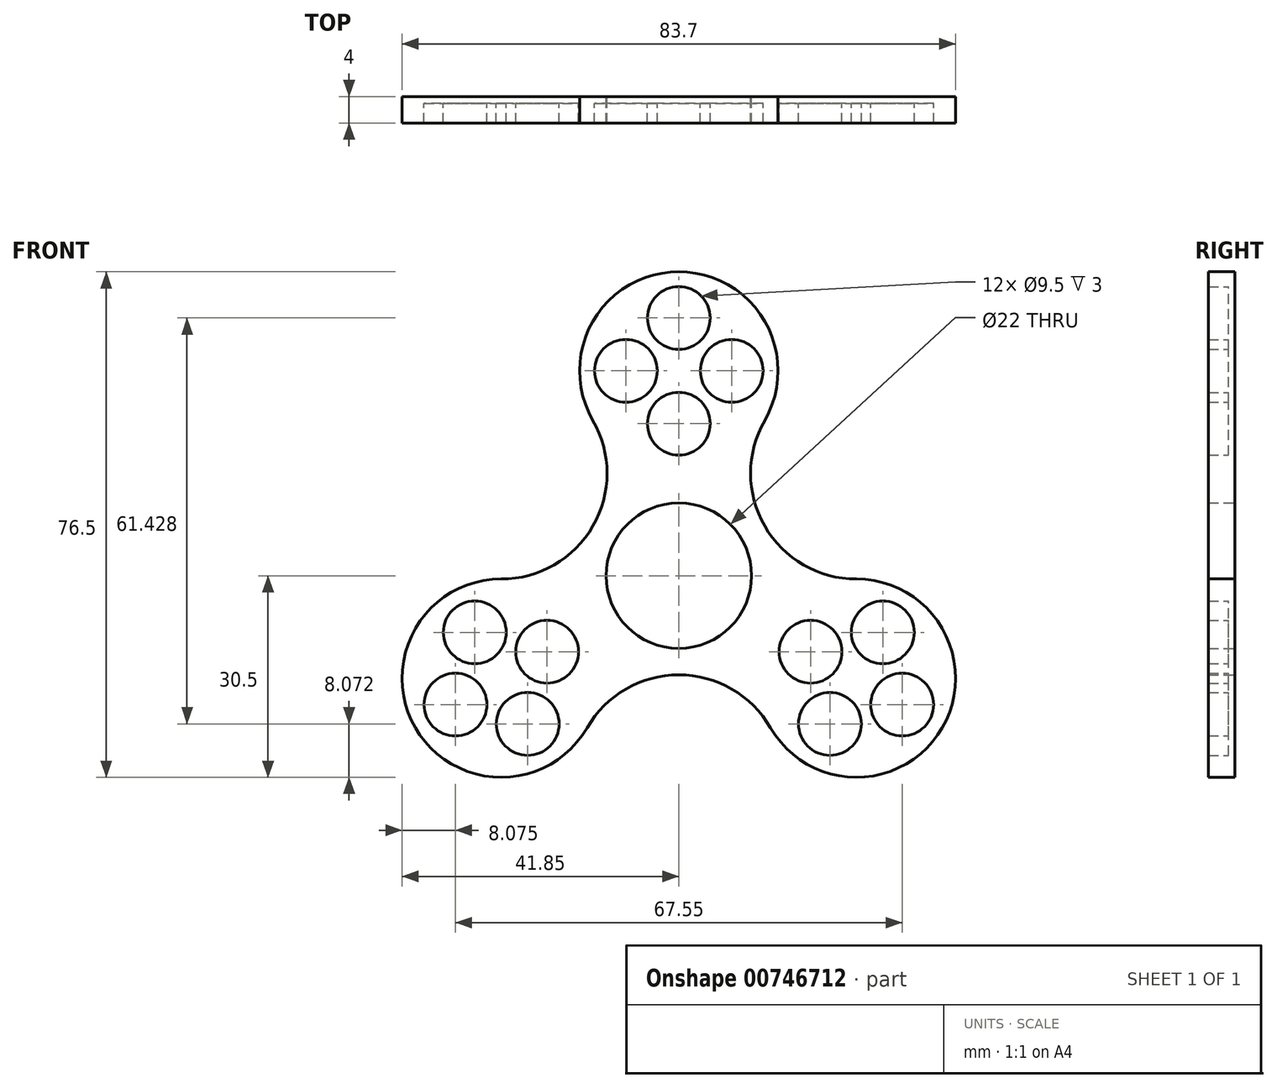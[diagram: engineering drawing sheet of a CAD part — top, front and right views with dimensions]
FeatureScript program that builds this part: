
annotation { "Feature Type Name" : "Feature", "Feature Type Description" : "" }
export const myFeature = defineFeature(function(context is Context, id is Id, definition is map)
    precondition{}
    {
        {
            var Q0;
            Q0=qCreatedBy(makeId("Front.planeOp"),FACE);
            var sketch = newSketch(context, id + "F0", { "sketchPlane" : qUnion([Q0])});
            skCircle(sketch, "E0", {"center": v(0, 0) * mm, "radius": 11 * mm});
            skArc(sketch, "E1.1.0", {"start": v(-26.85, -0.5) * mm, "mid": v(-39.84, -23) * mm, "end": v(-13.86, -23) * mm});
            skArc(sketch, "E1.2.0", {"start": v(13.86, -23) * mm, "mid": v(39.84, -23) * mm, "end": v(26.85, -0.5) * mm});
            skArc(sketch, "E2", {"start": v(-26.85, -0.5) * mm, "mid": v(-13, 7.5) * mm, "end": v(-13, 23.5) * mm});
            skArc(sketch, "E3.1.0", {"start": v(13.86, -23) * mm, "mid": v(0, -15) * mm, "end": v(-13.86, -23) * mm});
            skArc(sketch, "E3.2.0", {"start": v(13, 23.5) * mm, "mid": v(13, 7.5) * mm, "end": v(26.85, -0.5) * mm});
            skCircle(sketch, "E4", {"center": v(0, 23) * mm, "radius": 4.75 * mm});
            skCircle(sketch, "E5.1.0", {"center": v(8, 31) * mm, "radius": 4.75 * mm});
            skCircle(sketch, "E5.2.0", {"center": v(0, 39) * mm, "radius": 4.75 * mm});
            skCircle(sketch, "E5.3.0", {"center": v(-8, 31) * mm, "radius": 4.75 * mm});
            skPoint(sketch, "E5.center", {"position": v(0, 31) * mm});
            skCircle(sketch, "E6.1.0", {"center": v(-22.85, -22.43) * mm, "radius": 4.75 * mm});
            skCircle(sketch, "E6.1.1", {"center": v(-33.77, -19.5) * mm, "radius": 4.75 * mm});
            skCircle(sketch, "E6.1.2", {"center": v(-19.92, -11.5) * mm, "radius": 4.75 * mm});
            skCircle(sketch, "E6.1.3", {"center": v(-30.85, -8.57) * mm, "radius": 4.75 * mm});
            skCircle(sketch, "E6.2.0", {"center": v(30.85, -8.57) * mm, "radius": 4.75 * mm});
            skCircle(sketch, "E6.2.1", {"center": v(33.77, -19.5) * mm, "radius": 4.75 * mm});
            skCircle(sketch, "E6.2.2", {"center": v(19.92, -11.5) * mm, "radius": 4.75 * mm});
            skCircle(sketch, "E6.2.3", {"center": v(22.85, -22.43) * mm, "radius": 4.75 * mm});
            skArc(sketch, "E7", {"start": v(13, 23.5) * mm, "mid": v(0, 46) * mm, "end": v(-13, 23.5) * mm});
            skSolve(sketch);
        }
        {
            var Q0;
            Q0 = qSketchRegion(id + "F0", true);
            extrude(context, id + "F1", {"entities" : qUnion([Q0]), "depth" : 4 * mm, "offsetDistance" : 25 * mm});
        }
        {
            var Q0;
            Q0=makeQuery(id+"F0.imprint","IMPRINT",FACE,{"disambiguationData":[TD([[makeQuery(id+"F0.imprint","IMPRINT",EDGE,{"derivedFrom":sQuery(id+"F0.wireOp",EDGE,"E5.3.0")}),1.0]])]});
            var Q1;
            Q1=makeQuery(id+"F0.imprint","IMPRINT",FACE,{"disambiguationData":[TD([[makeQuery(id+"F0.imprint","IMPRINT",EDGE,{"derivedFrom":sQuery(id+"F0.wireOp",EDGE,"E5.2.0")}),1.0]])]});
            var Q2;
            Q2=makeQuery(id+"F0.imprint","IMPRINT",FACE,{"disambiguationData":[TD([[makeQuery(id+"F0.imprint","IMPRINT",EDGE,{"derivedFrom":sQuery(id+"F0.wireOp",EDGE,"E5.1.0")}),1.0]])]});
            var Q3;
            Q3=makeQuery(id+"F0.imprint","IMPRINT",FACE,{"disambiguationData":[TD([[makeQuery(id+"F0.imprint","IMPRINT",EDGE,{"derivedFrom":sQuery(id+"F0.wireOp",EDGE,"E4")}),1.0]])]});
            var Q4;
            Q4=makeQuery(id+"F0.imprint","IMPRINT",FACE,{"disambiguationData":[TD([[makeQuery(id+"F0.imprint","IMPRINT",EDGE,{"derivedFrom":sQuery(id+"F0.wireOp",EDGE,"E6.1.3")}),1.0]])]});
            var Q5;
            Q5=makeQuery(id+"F0.imprint","IMPRINT",FACE,{"disambiguationData":[TD([[makeQuery(id+"F0.imprint","IMPRINT",EDGE,{"derivedFrom":sQuery(id+"F0.wireOp",EDGE,"E6.1.1")}),1.0]])]});
            var Q6;
            Q6=makeQuery(id+"F0.imprint","IMPRINT",FACE,{"disambiguationData":[TD([[makeQuery(id+"F0.imprint","IMPRINT",EDGE,{"derivedFrom":sQuery(id+"F0.wireOp",EDGE,"E6.1.0")}),1.0]])]});
            var Q7;
            Q7=makeQuery(id+"F0.imprint","IMPRINT",FACE,{"disambiguationData":[TD([[makeQuery(id+"F0.imprint","IMPRINT",EDGE,{"derivedFrom":sQuery(id+"F0.wireOp",EDGE,"E6.1.2")}),1.0]])]});
            var Q8;
            Q8=makeQuery(id+"F0.imprint","IMPRINT",FACE,{"disambiguationData":[TD([[makeQuery(id+"F0.imprint","IMPRINT",EDGE,{"derivedFrom":sQuery(id+"F0.wireOp",EDGE,"E6.2.3")}),1.0]])]});
            var Q9;
            Q9=makeQuery(id+"F0.imprint","IMPRINT",FACE,{"disambiguationData":[TD([[makeQuery(id+"F0.imprint","IMPRINT",EDGE,{"derivedFrom":sQuery(id+"F0.wireOp",EDGE,"E6.2.2")}),1.0]])]});
            var Q10;
            Q10=makeQuery(id+"F0.imprint","IMPRINT",FACE,{"disambiguationData":[TD([[makeQuery(id+"F0.imprint","IMPRINT",EDGE,{"derivedFrom":sQuery(id+"F0.wireOp",EDGE,"E6.2.0")}),1.0]])]});
            var Q11;
            Q11=makeQuery(id+"F0.imprint","IMPRINT",FACE,{"disambiguationData":[TD([[makeQuery(id+"F0.imprint","IMPRINT",EDGE,{"derivedFrom":sQuery(id+"F0.wireOp",EDGE,"E6.2.1")}),1.0]])]});
            extrude(context, id + "F2", {"entities" : qUnion([Q0, Q1, Q2, Q3, Q4, Q5, Q6, Q7, Q8, Q9, Q10, Q11]), "operationType" : NewBodyOperationType.ADD, "depth" : 1 * mm, "offsetDistance" : 25 * mm});
        }
    });
